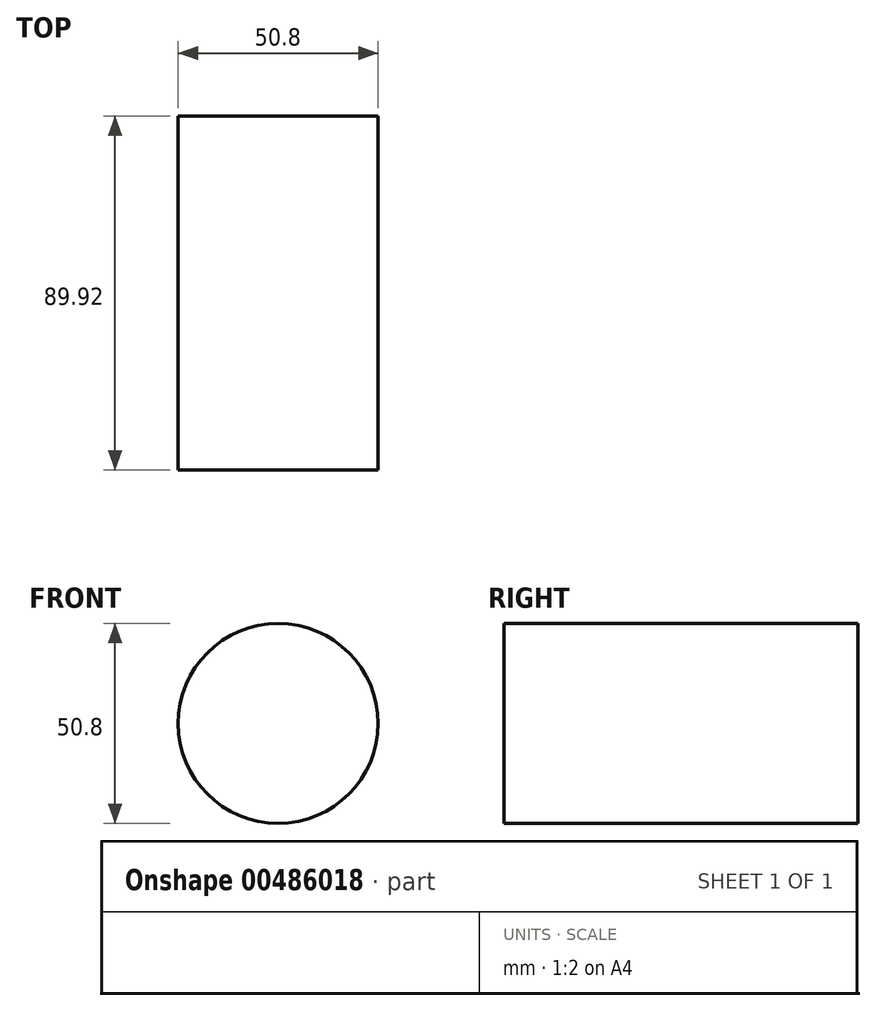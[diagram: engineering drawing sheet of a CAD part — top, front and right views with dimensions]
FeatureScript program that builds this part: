
annotation { "Feature Type Name" : "Feature", "Feature Type Description" : "" }
export const myFeature = defineFeature(function(context is Context, id is Id, definition is map)
    precondition{}
    {
        {
            var Q0;
            Q0=qCreatedBy(makeId("Front.planeOp"),FACE);
            var sketch = newSketch(context, id + "F0", { "sketchPlane" : qUnion([Q0])});
            skCircle(sketch, "E0", {"center": v(0, 0) * mm, "radius": 25.4 * mm});
            skSolve(sketch);
        }
        {
            var Q0;
            Q0 = qSketchRegion(id + "F0", true);
            extrude(context, id + "F1", {"entities" : qUnion([Q0]), "depth" : 89.92 * mm});
        }
    });
